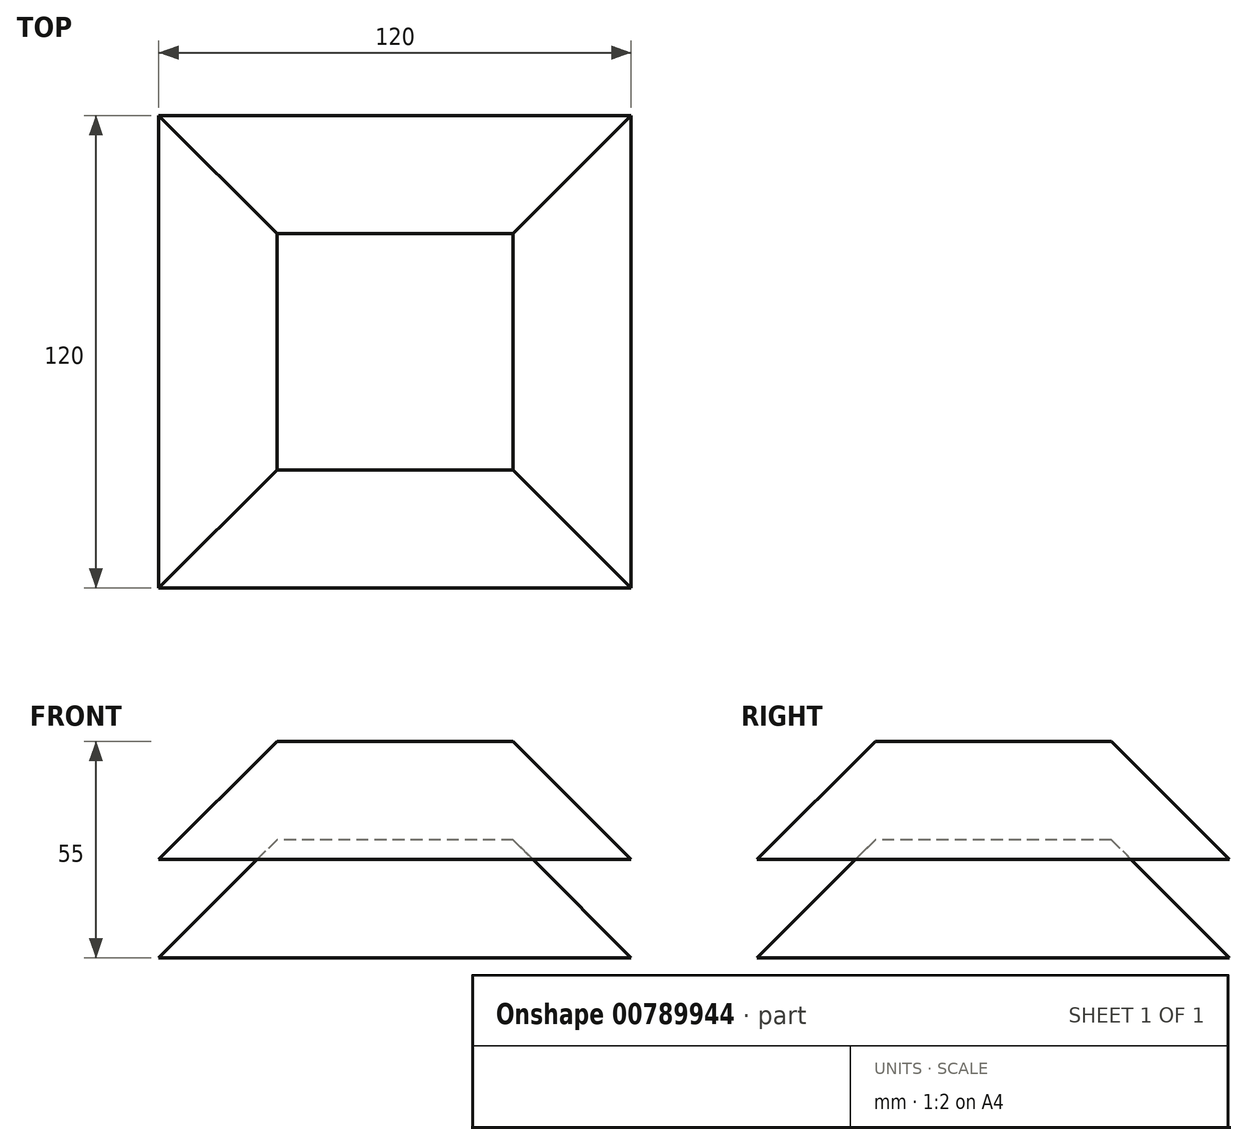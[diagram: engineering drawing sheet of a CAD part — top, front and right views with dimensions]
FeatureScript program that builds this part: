
annotation { "Feature Type Name" : "Feature", "Feature Type Description" : "" }
export const myFeature = defineFeature(function(context is Context, id is Id, definition is map)
    precondition{}
    {
        {
            var Q0;
            Q0=qCreatedBy(makeId("Top.planeOp"),FACE);
            var sketch = newSketch(context, id + "F0", { "sketchPlane" : qUnion([Q0])});
            skLineSegment(sketch, "E0.bottom", {"start": v(-30, 30) * mm, "end": v(30, 30) * mm});
            skLineSegment(sketch, "E0.top", {"start": v(-30, -30) * mm, "end": v(30, -30) * mm});
            skLineSegment(sketch, "E0.left", {"start": v(-30, 30) * mm, "end": v(-30, -30) * mm});
            skLineSegment(sketch, "E0.right", {"start": v(30, 30) * mm, "end": v(30, -30) * mm});
            skPoint(sketch, "E0.middle", {"position": v(0, 0) * mm});
            skSolve(sketch);
        }
        {
            var Q0;
            Q0=makeQuery(id+"F0.imprint","IMPRINT",FACE,{"disambiguationData":[TD([[makeQuery(id+"F0.imprint","IMPRINT",EDGE,{"derivedFrom":sQuery(id+"F0.wireOp",EDGE,"E0.bottom")}),-1.0]])]});
            extrude(context, id + "F1", {"entities" : qUnion([Q0]), "oppositeDirection" : true, "depth" : 30 * mm, "offsetDistance" : 25 * mm, "hasDraft" : true, "draftAngle" : 45 * degree});
        }
        {
            var Q0;
            Q0=qCreatedBy(makeId("Top.planeOp"),FACE);
            cPlane(context, id + "F2", {"entities" : qUnion([Q0]), "cplaneType" : CPlaneType.OFFSET, "offset" : 25 * mm, "width" : 150 * mm, "height" : 150 * mm});
        }
        {
            var Q0;
            Q0=qCreatedBy(id+"F2.planeOp",FACE);
            var sketch = newSketch(context, id + "F3", { "sketchPlane" : qUnion([Q0])});
            skLineSegment(sketch, "E1.0.0", {"start": v(-30, 30) * mm, "end": v(-30, -30) * mm});
            skLineSegment(sketch, "E1.0.1", {"start": v(-30, -30) * mm, "end": v(30, -30) * mm});
            skLineSegment(sketch, "E1.0.2", {"start": v(30, 30) * mm, "end": v(30, -30) * mm});
            skLineSegment(sketch, "E1.0.3", {"start": v(-30, 30) * mm, "end": v(30, 30) * mm});
            skSolve(sketch);
        }
        {
            var Q0;
            Q0=makeQuery(id+"F3.imprint","IMPRINT",FACE,{"disambiguationData":[TD([[makeQuery(id+"F3.imprint","IMPRINT",EDGE,{"derivedFrom":sQuery(id+"F3.wireOp",EDGE,"E1.0.0")}),1.0]])]});
            extrude(context, id + "F4", {"entities" : qUnion([Q0]), "oppositeDirection" : true, "depth" : 30 * mm, "offsetDistance" : 25 * mm, "hasDraft" : true, "draftAngle" : 45 * degree});
        }
    });
